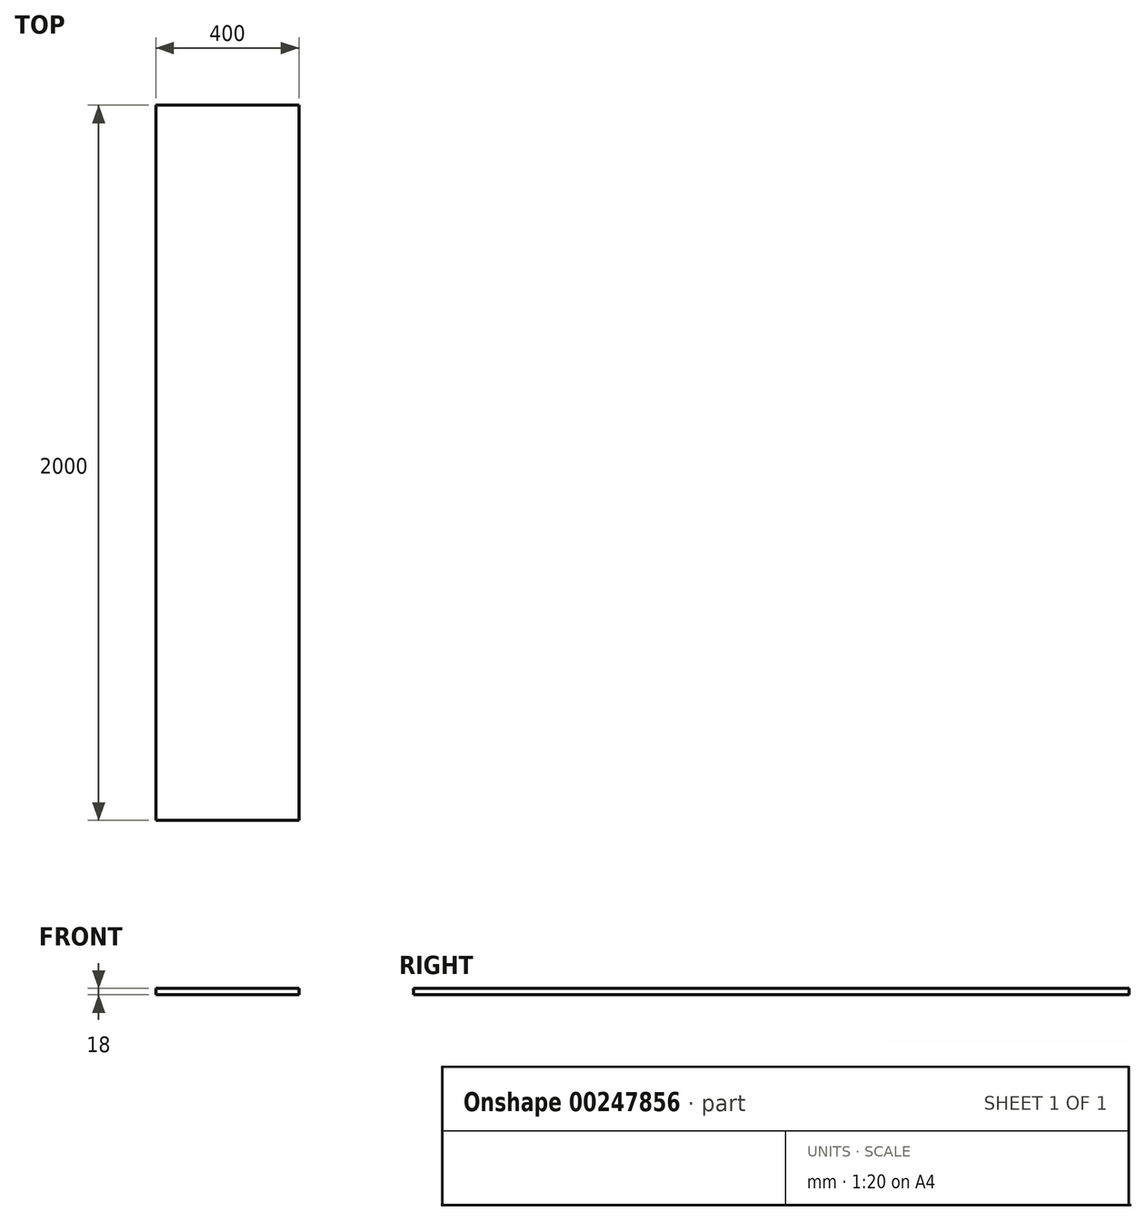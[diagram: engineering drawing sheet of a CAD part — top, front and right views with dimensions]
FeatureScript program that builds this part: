
annotation { "Feature Type Name" : "Feature", "Feature Type Description" : "" }
export const myFeature = defineFeature(function(context is Context, id is Id, definition is map)
    precondition{}
    {
        {
            var Q0;
            Q0=qCreatedBy(makeId("Top.planeOp"),FACE);
            var sketch = newSketch(context, id + "F1", { "sketchPlane" : qUnion([Q0])});
            skLineSegment(sketch, "E0.bottom", {"start": v(0, 0) * mm, "end": v(400, 0) * mm});
            skLineSegment(sketch, "E0.top", {"start": v(0, 2000) * mm, "end": v(400, 2000) * mm});
            skLineSegment(sketch, "E0.left", {"start": v(0, 0) * mm, "end": v(0, 2000) * mm});
            skLineSegment(sketch, "E0.right", {"start": v(400, 0) * mm, "end": v(400, 2000) * mm});
            skSolve(sketch);
        }
        {
            var Q0;
            Q0=makeQuery(id+"F1.imprint","IMPRINT",FACE,{"disambiguationData":[TD([[makeQuery(id+"F1.imprint","IMPRINT",EDGE,{"derivedFrom":sQuery(id+"F1.wireOp",EDGE,"E0.bottom")}),1.0]])]});
            extrude(context, id + "F0", {"entities" : qUnion([Q0]), "depth" : 18 * mm});
        }
    });
